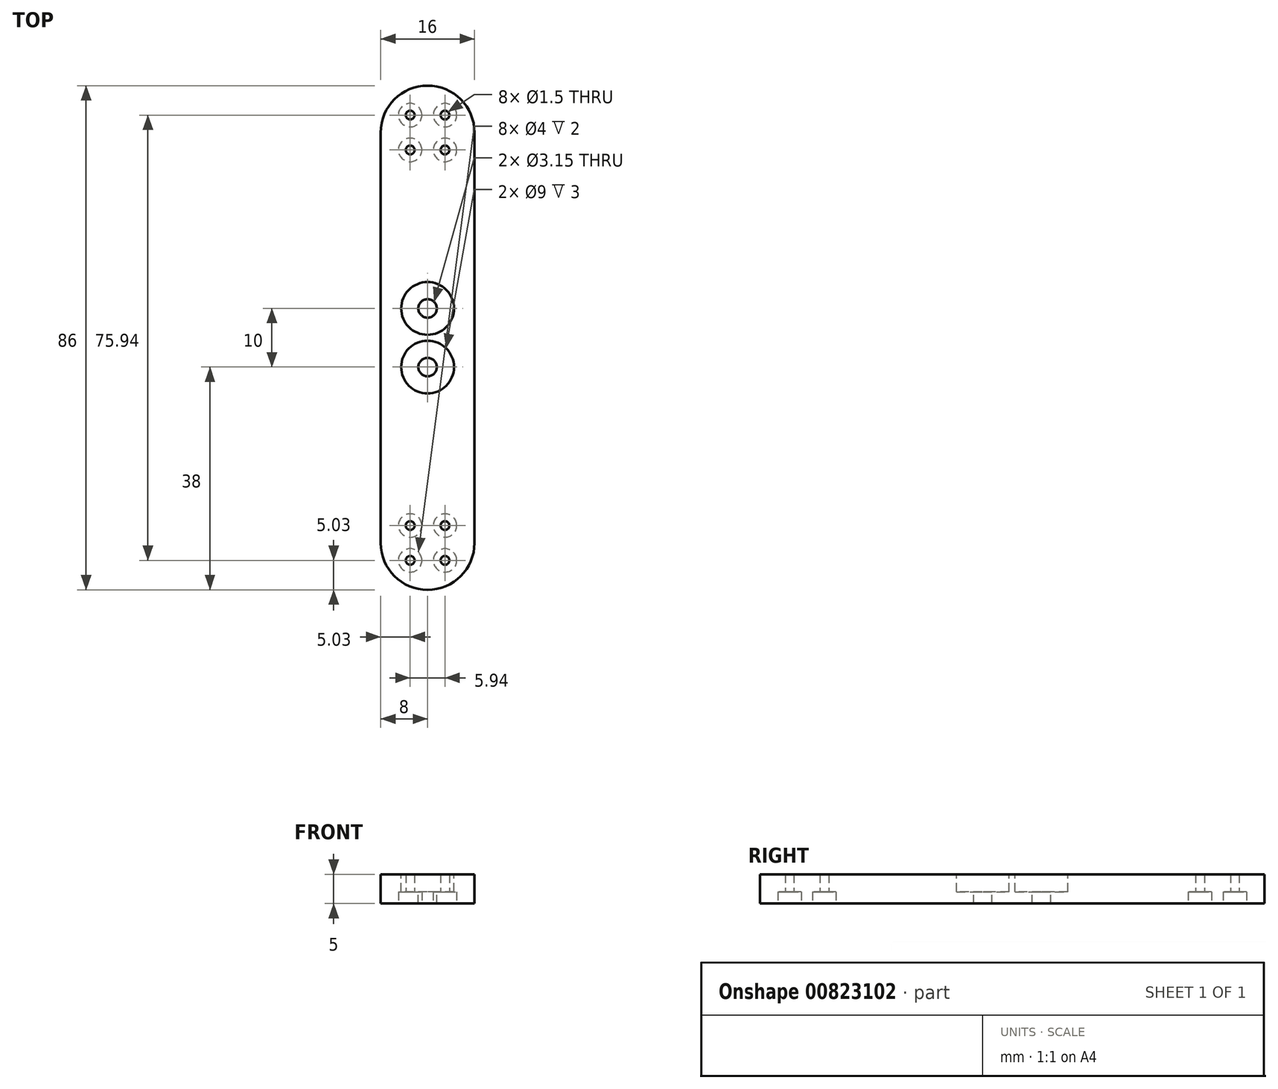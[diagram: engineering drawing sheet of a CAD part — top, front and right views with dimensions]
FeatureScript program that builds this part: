
annotation { "Feature Type Name" : "Feature", "Feature Type Description" : "" }
export const myFeature = defineFeature(function(context is Context, id is Id, definition is map)
    precondition{}
    {
        {
            var Q0;
            Q0=qCreatedBy(makeId("Top.planeOp"),FACE);
            var sketch = newSketch(context, id + "F0", { "sketchPlane" : qUnion([Q0])});
            skLineSegment(sketch, "E0", {"start": v(-8, 0) * mm, "end": v(-8, 35) * mm});
            skLineSegment(sketch, "E1", {"start": v(8, 0) * mm, "end": v(8, 35) * mm});
            skArc(sketch, "E2", {"start": v(-8, 35) * mm, "mid": v(0, 43) * mm, "end": v(8, 35) * mm});
            skLineSegment(sketch, "E3", {"start": v(-8, 0) * mm, "end": v(8, 0) * mm, "construction": true});
            skLineSegment(sketch, "E4", {"start": v(0, 35) * mm, "end": v(0, 24.43) * mm, "construction": true});
            skLineSegment(sketch, "E5", {"start": v(0, 24.43) * mm, "end": v(0, 35) * mm, "construction": true});
            skLineSegment(sketch, "E6", {"start": v(0, 35) * mm, "end": v(20.9, 35) * mm, "construction": true});
            skLineSegment(sketch, "E7.MirrorCS", {"start": v(8, 0) * mm, "end": v(8, -35) * mm});
            skLineSegment(sketch, "E8.MirrorCS", {"start": v(-8, 0) * mm, "end": v(-8, -35) * mm});
            skArc(sketch, "E9.MirrorCS", {"start": v(-8, -35) * mm, "mid": v(0, -43) * mm, "end": v(8, -35) * mm});
            skLineSegment(sketch, "E10.MirrorCS", {"start": v(0, -35) * mm, "end": v(20.9, -35) * mm, "construction": true});
            skLineSegment(sketch, "E11.MirrorCS", {"start": v(0, -24.43) * mm, "end": v(0, -35) * mm, "construction": true});
            skCircle(sketch, "E12", {"center": v(0, 35) * mm, "radius": 4.2 * mm, "construction": true});
            skCircle(sketch, "E13", {"center": v(2.97, 37.97) * mm, "radius": 0.75 * mm});
            skLineSegment(sketch, "E14", {"start": v(0, 35) * mm, "end": v(2.97, 37.97) * mm, "construction": true});
            skCircle(sketch, "E15.MirrorC", {"center": v(2.97, 32.03) * mm, "radius": 0.75 * mm});
            skCircle(sketch, "E16.MirrorC", {"center": v(-2.97, 32.03) * mm, "radius": 0.75 * mm});
            skCircle(sketch, "E17.MirrorC", {"center": v(-2.97, 37.97) * mm, "radius": 0.75 * mm});
            skCircle(sketch, "E18.MirrorC", {"center": v(-2.97, -32.03) * mm, "radius": 0.75 * mm});
            skCircle(sketch, "E19.MirrorC", {"center": v(2.97, -32.03) * mm, "radius": 0.75 * mm});
            skCircle(sketch, "E20.MirrorC", {"center": v(-2.97, -37.97) * mm, "radius": 0.75 * mm});
            skCircle(sketch, "E21.MirrorC", {"center": v(2.97, -37.97) * mm, "radius": 0.75 * mm});
            skCircle(sketch, "E22.MirrorC", {"center": v(0, -35) * mm, "radius": 4.2 * mm, "construction": true});
            skSolve(sketch);
        }
        {
            var Q0;
            Q0 = qSketchRegion(id + "F0", true);
            extrude(context, id + "F1", {"entities" : qUnion([Q0]), "depth" : 5 * mm, "offsetDistance" : 25 * mm});
        }
        {
            var Q0;
            Q0=makeQuery(id+"F1.opExtrude","CAP_FACE",FACE,{"disambiguationData":[OSD([sQuery(id+"F0.wireOp",EDGE,"E0"),sQuery(id+"F0.wireOp",EDGE,"E1"),sQuery(id+"F0.wireOp",EDGE,"E2"),sQuery(id+"F0.wireOp",EDGE,"E7.MirrorCS"),sQuery(id+"F0.wireOp",EDGE,"E8.MirrorCS"),sQuery(id+"F0.wireOp",EDGE,"E9.MirrorCS"),sQuery(id+"F0.wireOp",EDGE,"E13"),sQuery(id+"F0.wireOp",EDGE,"E15.MirrorC"),sQuery(id+"F0.wireOp",EDGE,"E16.MirrorC"),sQuery(id+"F0.wireOp",EDGE,"E17.MirrorC"),sQuery(id+"F0.wireOp",EDGE,"E18.MirrorC"),sQuery(id+"F0.wireOp",EDGE,"E19.MirrorC"),sQuery(id+"F0.wireOp",EDGE,"E20.MirrorC"),sQuery(id+"F0.wireOp",EDGE,"E21.MirrorC")])],"isStart":false});
            var sketch = newSketch(context, id + "F2", { "sketchPlane" : qUnion([Q0])});
            skCircle(sketch, "E23", {"center": v(0, 5) * mm, "radius": 1.57 * mm});
            skLineSegment(sketch, "E24", {"start": v(0, 0) * mm, "end": v(0, 8.86) * mm, "construction": true});
            skLineSegment(sketch, "E25", {"start": v(0, 8.86) * mm, "end": v(0, 0) * mm, "construction": true});
            skLineSegment(sketch, "E26", {"start": v(5.05, 0) * mm, "end": v(0, 0) * mm, "construction": true});
            skCircle(sketch, "E27.MirrorC", {"center": v(0, -5) * mm, "radius": 1.57 * mm});
            skSolve(sketch);
        }
        {
            var Q0;
            Q0 = qSketchRegion(id + "F2", true);
            extrude(context, id + "F3", {"entities" : qUnion([Q0]), "operationType" : NewBodyOperationType.REMOVE, "endBound" : BoundingType.THROUGH_ALL, "oppositeDirection" : true, "depth" : 25 * mm, "offsetDistance" : 25 * mm});
        }
        {
            var Q0;
            Q0=makeQuery(id+"F1.opExtrude","CAP_FACE",FACE,{"disambiguationData":[OSD([sQuery(id+"F0.wireOp",EDGE,"E0"),sQuery(id+"F0.wireOp",EDGE,"E1"),sQuery(id+"F0.wireOp",EDGE,"E2"),sQuery(id+"F0.wireOp",EDGE,"E7.MirrorCS"),sQuery(id+"F0.wireOp",EDGE,"E8.MirrorCS"),sQuery(id+"F0.wireOp",EDGE,"E9.MirrorCS"),sQuery(id+"F0.wireOp",EDGE,"E13"),sQuery(id+"F0.wireOp",EDGE,"E15.MirrorC"),sQuery(id+"F0.wireOp",EDGE,"E16.MirrorC"),sQuery(id+"F0.wireOp",EDGE,"E17.MirrorC"),sQuery(id+"F0.wireOp",EDGE,"E18.MirrorC"),sQuery(id+"F0.wireOp",EDGE,"E19.MirrorC"),sQuery(id+"F0.wireOp",EDGE,"E20.MirrorC"),sQuery(id+"F0.wireOp",EDGE,"E21.MirrorC")])],"isStart":false});
            var sketch = newSketch(context, id + "F4", { "sketchPlane" : qUnion([Q0])});
            skCircle(sketch, "E28", {"center": v(0, 5) * mm, "radius": 4.5 * mm});
            skCircle(sketch, "E29", {"center": v(0, -5) * mm, "radius": 4.5 * mm});
            skSolve(sketch);
        }
        {
            var Q0;
            Q0 = qSketchRegion(id + "F4", true);
            extrude(context, id + "F5", {"entities" : qUnion([Q0]), "operationType" : NewBodyOperationType.REMOVE, "oppositeDirection" : true, "depth" : 3 * mm, "offsetDistance" : 25 * mm});
        }
        {
            var Q0;
            Q0=makeQuery(id+"F1.opExtrude","CAP_FACE",FACE,{"disambiguationData":[OSD([sQuery(id+"F0.wireOp",EDGE,"E0"),sQuery(id+"F0.wireOp",EDGE,"E1"),sQuery(id+"F0.wireOp",EDGE,"E2"),sQuery(id+"F0.wireOp",EDGE,"E7.MirrorCS"),sQuery(id+"F0.wireOp",EDGE,"E8.MirrorCS"),sQuery(id+"F0.wireOp",EDGE,"E9.MirrorCS"),sQuery(id+"F0.wireOp",EDGE,"E13"),sQuery(id+"F0.wireOp",EDGE,"E15.MirrorC"),sQuery(id+"F0.wireOp",EDGE,"E16.MirrorC"),sQuery(id+"F0.wireOp",EDGE,"E17.MirrorC"),sQuery(id+"F0.wireOp",EDGE,"E18.MirrorC"),sQuery(id+"F0.wireOp",EDGE,"E19.MirrorC"),sQuery(id+"F0.wireOp",EDGE,"E20.MirrorC"),sQuery(id+"F0.wireOp",EDGE,"E21.MirrorC")])],"isStart":true});
            var sketch = newSketch(context, id + "F6", { "sketchPlane" : qUnion([Q0])});
            skCircle(sketch, "E30", {"center": v(-2.97, 37.97) * mm, "radius": 2 * mm});
            skLineSegment(sketch, "E31", {"start": v(0, 0) * mm, "end": v(0, 35) * mm, "construction": true});
            skLineSegment(sketch, "E32", {"start": v(0, 35) * mm, "end": v(13.56, 35) * mm, "construction": true});
            skCircle(sketch, "E33.MirrorC", {"center": v(2.97, 37.97) * mm, "radius": 2 * mm});
            skCircle(sketch, "E34.MirrorC", {"center": v(2.97, 32.03) * mm, "radius": 2 * mm});
            skCircle(sketch, "E35.MirrorC", {"center": v(-2.97, 32.03) * mm, "radius": 2 * mm});
            skLineSegment(sketch, "E36", {"start": v(0, 0) * mm, "end": v(13.4, 0) * mm, "construction": true});
            skCircle(sketch, "E37.MirrorC", {"center": v(-2.97, -32.03) * mm, "radius": 2 * mm});
            skCircle(sketch, "E38.MirrorC", {"center": v(-2.97, -37.97) * mm, "radius": 2 * mm});
            skCircle(sketch, "E39.MirrorC", {"center": v(2.97, -37.97) * mm, "radius": 2 * mm});
            skCircle(sketch, "E40.MirrorC", {"center": v(2.97, -32.03) * mm, "radius": 2 * mm});
            skSolve(sketch);
        }
        {
            var Q0;
            Q0 = qSketchRegion(id + "F6", true);
            extrude(context, id + "F7", {"entities" : qUnion([Q0]), "operationType" : NewBodyOperationType.REMOVE, "oppositeDirection" : true, "depth" : 2 * mm, "offsetDistance" : 25 * mm});
        }
    });
